SOLIDWORKS PART (.sldprt)
format: sldprt  version: not decoded by parser v0  size: 104,448 bytes
history: native  units: mm
features: plane x8, sketch x5, cut_extrude x3, extrude x2, material x1 (+10 scaffold rows collapsed)
feature tree (29):
  scaffold x10  (default folders/planes/origin — collapsed)
  material  "材质 <未指定>"
  plane  "前视基准面"
  plane  "上视基准面"
  plane  "右视基准面"
  plane  "基准面4"
  sketch  "草图1"
  extrude  "凸台-拉伸1"  Depth=22mm
  plane  "基准面5"
  sketch  "草图2"
  extrude  "凸台-拉伸2"  Depth=10mm
  plane  "基准面6"
  sketch  "草图3"
  cut_extrude  "切除-拉伸1"  Depth=0.1mm
  plane  "基准面7"
  sketch  "草图4"
  cut_extrude  "切除-拉伸2"  Depth=0.1mm
  plane  "基准面8"
  sketch  "草图5"
  cut_extrude  "切除-拉伸3"  Depth=0.1mm
decode coverage: 5 of 10 modeling features carry decoded parameters
note: suppression state not decoded; provenance and decode notes live in map.json
